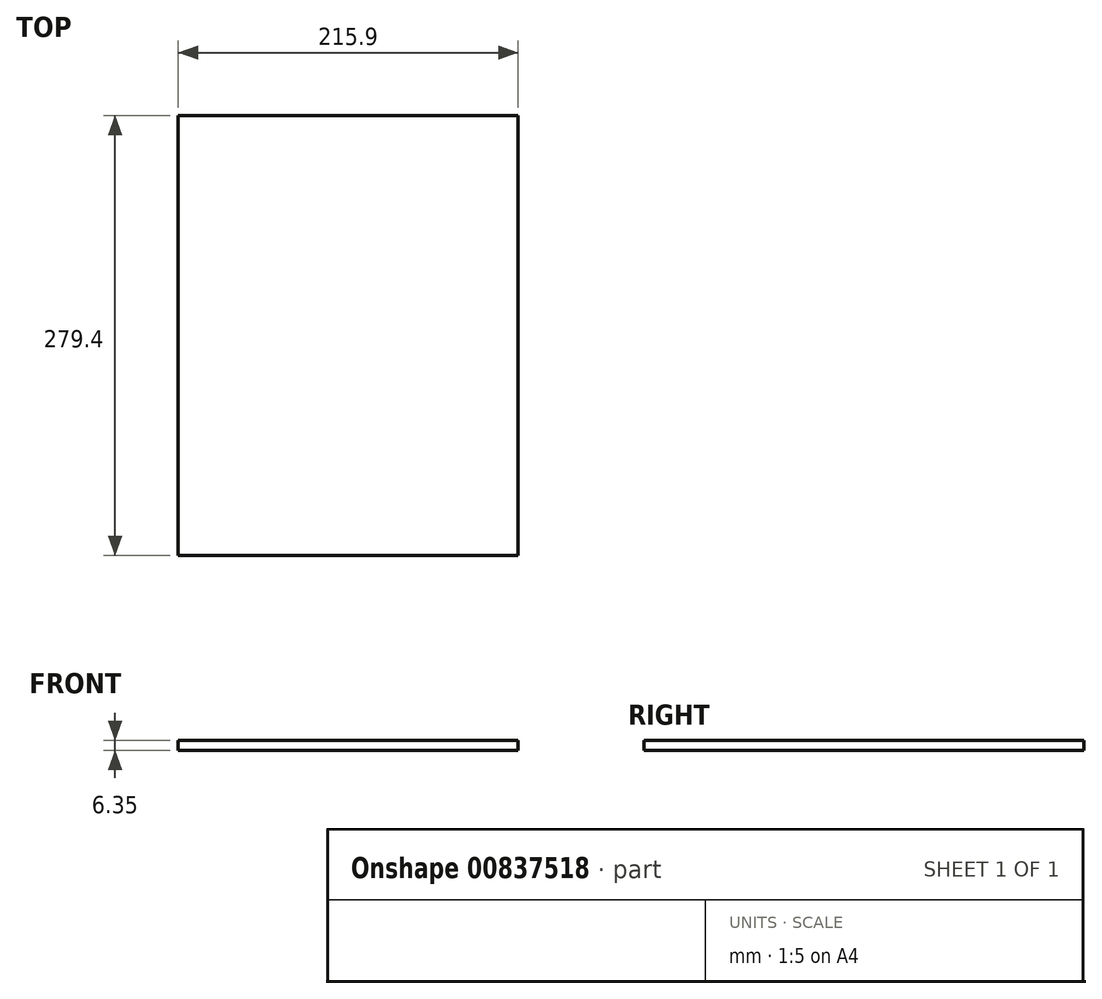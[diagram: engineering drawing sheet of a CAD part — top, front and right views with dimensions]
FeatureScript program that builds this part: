
annotation { "Feature Type Name" : "Feature", "Feature Type Description" : "" }
export const myFeature = defineFeature(function(context is Context, id is Id, definition is map)
    precondition{}
    {
        {
            var Q0;
            Q0=qCreatedBy(makeId("Top.planeOp"),FACE);
            var sketch = newSketch(context, id + "F0", { "sketchPlane" : qUnion([Q0])});
            skLineSegment(sketch, "E0.bottom", {"start": v(95.39, 207.67) * mm, "end": v(-120.51, 207.67) * mm});
            skLineSegment(sketch, "E0.top", {"start": v(95.39, -71.73) * mm, "end": v(-120.51, -71.73) * mm});
            skLineSegment(sketch, "E0.left", {"start": v(95.39, 207.67) * mm, "end": v(95.39, -71.73) * mm});
            skLineSegment(sketch, "E0.right", {"start": v(-120.51, 207.67) * mm, "end": v(-120.51, -71.73) * mm});
            skSolve(sketch);
        }
        {
            var Q0;
            Q0=makeQuery(id+"F0.imprint","IMPRINT",FACE,{"disambiguationData":[TD([[makeQuery(id+"F0.imprint","IMPRINT",EDGE,{"derivedFrom":sQuery(id+"F0.wireOp",EDGE,"E0.bottom")}),1.0]])]});
            extrude(context, id + "F1", {"entities" : qUnion([Q0]), "depth" : 6.35 * mm, "offsetDistance" : 25.4 * mm});
        }
    });
